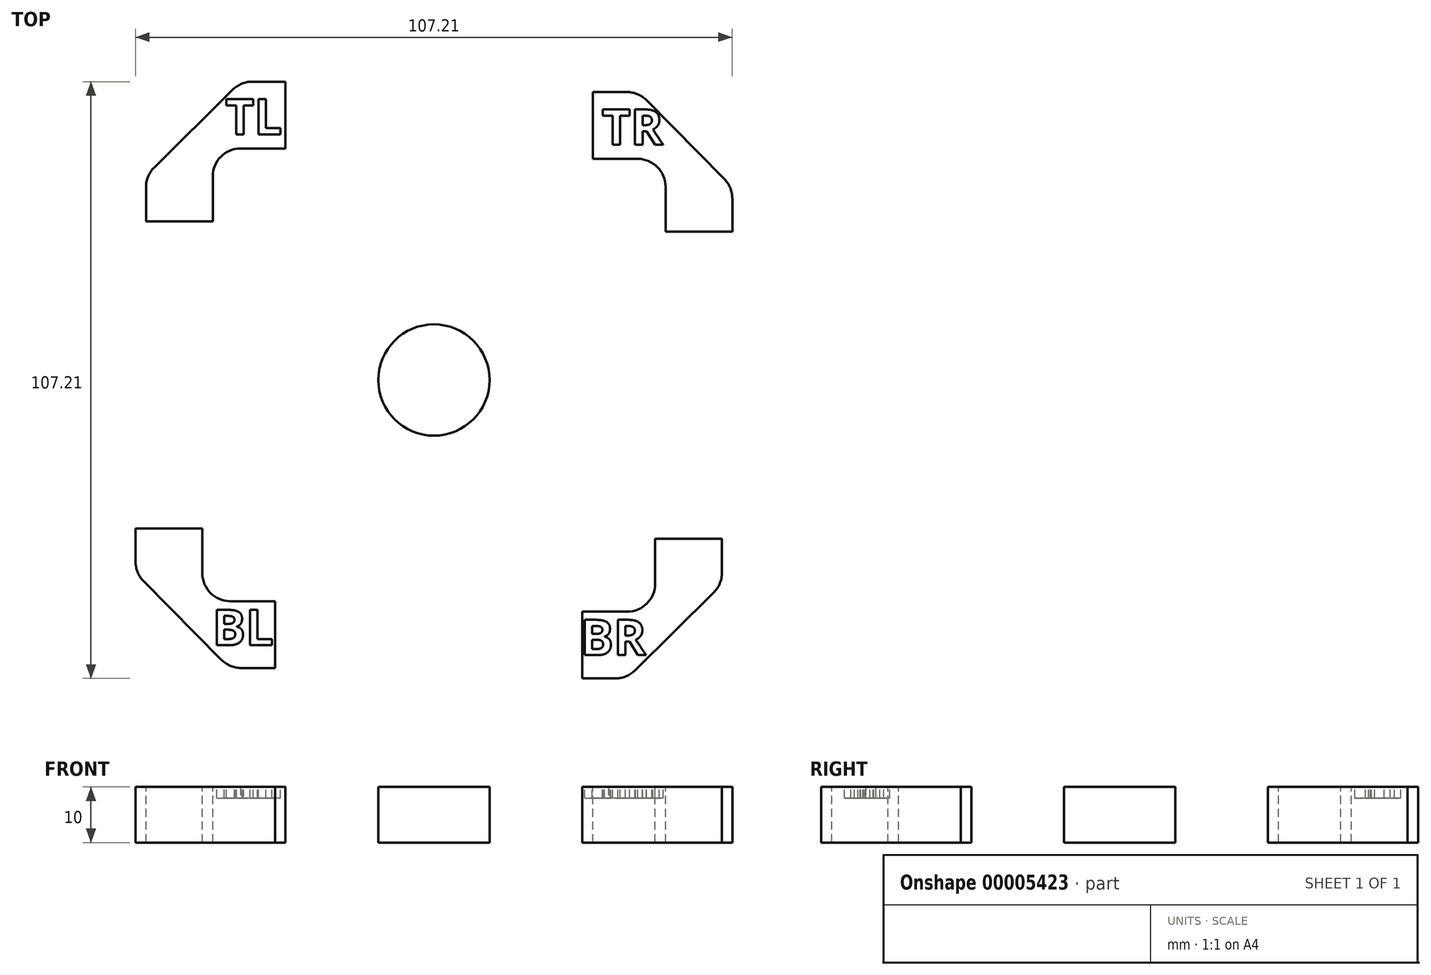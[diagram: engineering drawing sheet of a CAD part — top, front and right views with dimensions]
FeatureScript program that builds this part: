
annotation { "Feature Type Name" : "Feature", "Feature Type Description" : "" }
export const myFeature = defineFeature(function(context is Context, id is Id, definition is map)
    precondition{}
    {
        {
            var Q0;
            Q0=qCreatedBy(makeId("Top.planeOp"),FACE);
            var sketch = newSketch(context, id + "F0", { "sketchPlane" : qUnion([Q0])});
            skPoint(sketch, "E0.rect.middle", {"position": v(0, 0) * mm});
            skLineSegment(sketch, "E1.top", {"start": v(28.56, 51.77) * mm, "end": v(34.68, 51.77) * mm});
            skLineSegment(sketch, "E2.bottom", {"start": v(34.68, 51.77) * mm, "end": v(28.56, 51.77) * mm});
            skLineSegment(sketch, "E2.top", {"start": v(53.64, 26.7) * mm, "end": v(41.64, 26.7) * mm});
            skLineSegment(sketch, "E2.left", {"start": v(53.64, 32.66) * mm, "end": v(53.64, 26.7) * mm});
            skLineSegment(sketch, "E2.right", {"start": v(28.56, 51.77) * mm, "end": v(28.56, 39.77) * mm});
            skLineSegment(sketch, "E3.bottom", {"start": v(28.56, 39.77) * mm, "end": v(36.64, 39.77) * mm});
            skLineSegment(sketch, "E3.right", {"start": v(41.64, 34.77) * mm, "end": v(41.64, 26.7) * mm});
            skPoint(sketch, "E4.orphan", {"position": v(44.55, 51.77) * mm});
            skPoint(sketch, "E5.orphan", {"position": v(53.64, 51.77) * mm});
            skPoint(sketch, "E6.visualSharp", {"position": v(41.64, 39.77) * mm});
            skArc(sketch, "E6.filletArc", {"start": v(41.64, 34.77) * mm, "mid": v(40.18, 38.3) * mm, "end": v(36.64, 39.77) * mm});
            skPoint(sketch, "E7.visualSharp", {"position": v(36.67, 51.77) * mm});
            skArc(sketch, "E7.filletArc", {"start": v(38.22, 50.3) * mm, "mid": v(36.6, 51.4) * mm, "end": v(34.68, 51.77) * mm});
            skPoint(sketch, "E8.visualSharp", {"position": v(53.64, 34.62) * mm});
            skArc(sketch, "E8.filletArc", {"start": v(53.64, 32.66) * mm, "mid": v(53.27, 34.55) * mm, "end": v(52.21, 36.16) * mm});
            skLineSegment(sketch, "E9", {"start": v(38.22, 50.3) * mm, "end": v(52.21, 36.16) * mm});
            skPoint(sketch, "E10.1.0", {"position": v(-51.7, 36.67) * mm});
            skPoint(sketch, "E10.1.1", {"position": v(-39.7, 41.64) * mm});
            skPoint(sketch, "E10.1.2", {"position": v(-51.7, 44.55) * mm});
            skLineSegment(sketch, "E10.1.3", {"start": v(-50.24, 38.22) * mm, "end": v(-36.09, 52.21) * mm});
            skLineSegment(sketch, "E10.1.4", {"start": v(-34.7, 41.64) * mm, "end": v(-26.62, 41.64) * mm});
            skLineSegment(sketch, "E10.1.5", {"start": v(-51.7, 28.56) * mm, "end": v(-39.7, 28.56) * mm});
            skLineSegment(sketch, "E10.1.6", {"start": v(-39.7, 28.56) * mm, "end": v(-39.7, 36.64) * mm});
            skLineSegment(sketch, "E10.1.7", {"start": v(-26.62, 53.64) * mm, "end": v(-26.62, 41.64) * mm});
            skLineSegment(sketch, "E10.1.8", {"start": v(-32.59, 53.64) * mm, "end": v(-26.62, 53.64) * mm});
            skLineSegment(sketch, "E10.1.9", {"start": v(-51.7, 34.68) * mm, "end": v(-51.7, 28.56) * mm});
            skPoint(sketch, "E10.1.10", {"position": v(-34.55, 53.64) * mm});
            skPoint(sketch, "E10.1.11", {"position": v(-51.7, 53.64) * mm});
            skArc(sketch, "E10.1.12", {"start": v(-50.24, 38.22) * mm, "mid": v(-51.32, 36.6) * mm, "end": v(-51.7, 34.68) * mm});
            skArc(sketch, "E10.1.13", {"start": v(-32.59, 53.64) * mm, "mid": v(-34.48, 53.27) * mm, "end": v(-36.09, 52.21) * mm});
            skArc(sketch, "E10.1.14", {"start": v(-34.7, 41.64) * mm, "mid": v(-38.24, 40.18) * mm, "end": v(-39.7, 36.64) * mm});
            skPoint(sketch, "E10.2.0", {"position": v(-36.6, -51.7) * mm});
            skPoint(sketch, "E10.2.1", {"position": v(-41.57, -39.7) * mm});
            skPoint(sketch, "E10.2.2", {"position": v(-44.48, -51.7) * mm});
            skLineSegment(sketch, "E10.2.3", {"start": v(-38.15, -50.24) * mm, "end": v(-52.14, -36.09) * mm});
            skLineSegment(sketch, "E10.2.4", {"start": v(-41.57, -34.7) * mm, "end": v(-41.57, -26.62) * mm});
            skLineSegment(sketch, "E10.2.5", {"start": v(-28.5, -51.7) * mm, "end": v(-28.5, -39.7) * mm});
            skLineSegment(sketch, "E10.2.6", {"start": v(-28.5, -39.7) * mm, "end": v(-36.57, -39.7) * mm});
            skLineSegment(sketch, "E10.2.7", {"start": v(-53.57, -26.62) * mm, "end": v(-41.57, -26.62) * mm});
            skLineSegment(sketch, "E10.2.8", {"start": v(-53.57, -32.59) * mm, "end": v(-53.57, -26.62) * mm});
            skLineSegment(sketch, "E10.2.9", {"start": v(-34.61, -51.7) * mm, "end": v(-28.5, -51.7) * mm});
            skPoint(sketch, "E10.2.10", {"position": v(-53.57, -34.55) * mm});
            skPoint(sketch, "E10.2.11", {"position": v(-53.57, -51.7) * mm});
            skArc(sketch, "E10.2.12", {"start": v(-38.15, -50.24) * mm, "mid": v(-36.53, -51.32) * mm, "end": v(-34.61, -51.7) * mm});
            skArc(sketch, "E10.2.13", {"start": v(-53.57, -32.59) * mm, "mid": v(-53.2, -34.48) * mm, "end": v(-52.14, -36.09) * mm});
            skArc(sketch, "E10.2.14", {"start": v(-41.57, -34.7) * mm, "mid": v(-40.1, -38.24) * mm, "end": v(-36.57, -39.7) * mm});
            skPoint(sketch, "E10.3.0", {"position": v(51.77, -36.6) * mm});
            skPoint(sketch, "E10.3.1", {"position": v(39.77, -41.57) * mm});
            skPoint(sketch, "E10.3.2", {"position": v(51.77, -44.48) * mm});
            skLineSegment(sketch, "E10.3.3", {"start": v(50.3, -38.15) * mm, "end": v(36.16, -52.14) * mm});
            skLineSegment(sketch, "E10.3.4", {"start": v(34.77, -41.57) * mm, "end": v(26.7, -41.57) * mm});
            skLineSegment(sketch, "E10.3.5", {"start": v(51.77, -28.5) * mm, "end": v(39.77, -28.5) * mm});
            skLineSegment(sketch, "E10.3.6", {"start": v(39.77, -28.5) * mm, "end": v(39.77, -36.57) * mm});
            skLineSegment(sketch, "E10.3.7", {"start": v(26.7, -53.57) * mm, "end": v(26.7, -41.57) * mm});
            skLineSegment(sketch, "E10.3.8", {"start": v(32.66, -53.57) * mm, "end": v(26.7, -53.57) * mm});
            skLineSegment(sketch, "E10.3.9", {"start": v(51.77, -34.61) * mm, "end": v(51.77, -28.5) * mm});
            skPoint(sketch, "E10.3.10", {"position": v(34.62, -53.57) * mm});
            skPoint(sketch, "E10.3.11", {"position": v(51.77, -53.57) * mm});
            skArc(sketch, "E10.3.12", {"start": v(50.3, -38.15) * mm, "mid": v(51.4, -36.53) * mm, "end": v(51.77, -34.61) * mm});
            skArc(sketch, "E10.3.13", {"start": v(32.66, -53.57) * mm, "mid": v(34.55, -53.2) * mm, "end": v(36.16, -52.14) * mm});
            skArc(sketch, "E10.3.14", {"start": v(34.77, -41.57) * mm, "mid": v(38.3, -40.1) * mm, "end": v(39.77, -36.57) * mm});
            skPoint(sketch, "E10.center", {"position": v(0.04, 0.04) * mm});
            skCircle(sketch, "E11", {"center": v(0.04, 0.04) * mm, "radius": 10 * mm});
            skText(sketch, "E12", { "text": "TL", "fontName": "OpenSans-Bold.ttf"});
            skText(sketch, "E13", { "text": "TR", "fontName": "OpenSans-Bold.ttf"});
            skText(sketch, "E14", { "text": "BL", "fontName": "OpenSans-Bold.ttf"});
            skText(sketch, "E15", { "text": "BR", "fontName": "OpenSans-Bold.ttf"});
            const initialGuessF0  = {"E12": [-0.03741, 0.04417, 1, 0, 0.0064], "E13": [0.03022, 0.0423, 1, 0, 0.0064], "E14": [-0.03977, -0.0476, 1, 0, 0.0064], "E15": [0.02633, -0.0494, 1, 0, 0.0064]};
            skSetInitialGuess(sketch, initialGuessF0);
            skSolve(sketch);
        }
        {
            var Q0;
            Q0=makeQuery(id+"F0.imprint","IMPRINT",FACE,{"disambiguationData":[TD([[makeQuery(id+"F0.imprint","IMPRINT",EDGE,{"derivedFrom":sQuery(id+"F0.wireOp",EDGE,"E10.1.3")}),-1.0]])]});
            var Q1;
            Q1=makeQuery(id+"F0.imprint","IMPRINT",FACE,{"disambiguationData":[TD([[makeQuery(id+"F0.imprint","IMPRINT",EDGE,{"derivedFrom":sQuery(id+"F0.wireOp",EDGE,"E2.bottom")}),1.0]])]});
            var Q2;
            Q2=makeQuery(id+"F0.imprint","IMPRINT",FACE,{"disambiguationData":[TD([[makeQuery(id+"F0.imprint","IMPRINT",EDGE,{"derivedFrom":sQuery(id+"F0.wireOp",EDGE,"E10.2.3")}),-1.0]])]});
            var Q3;
            Q3=makeQuery(id+"F0.imprint","IMPRINT",FACE,{"disambiguationData":[TD([[makeQuery(id+"F0.imprint","IMPRINT",EDGE,{"derivedFrom":sQuery(id+"F0.wireOp",EDGE,"E10.3.3")}),-1.0]])]});
            var Q4;
            Q4=makeQuery(id+"F0.imprint","IMPRINT",FACE,{"disambiguationData":[TD([[makeQuery(id+"F0.imprint","IMPRINT",EDGE,{"derivedFrom":sQuery(id+"F0.wireOp",EDGE,"E11")}),1.0]])]});
            var Q5;
            Q5=makeQuery(id+"F0.imprint","IMPRINT",FACE,{"disambiguationData":[TD([[makeQuery(id+"F0.imprint","IMPRINT",EDGE,{"derivedFrom":sQuery(id+"F0.wireOp",EDGE,"E12.sketch_text.stroke-8")}),-1.0]])]});
            var Q6;
            Q6=makeQuery(id+"F0.imprint","IMPRINT",FACE,{"disambiguationData":[TD([[makeQuery(id+"F0.imprint","IMPRINT",EDGE,{"derivedFrom":sQuery(id+"F0.wireOp",EDGE,"E12.sketch_text.stroke-0")}),-1.0]])]});
            var Q7;
            Q7=makeQuery(id+"F0.imprint","IMPRINT",FACE,{"disambiguationData":[TD([[makeQuery(id+"F0.imprint","IMPRINT",EDGE,{"derivedFrom":sQuery(id+"F0.wireOp",EDGE,"E13.sketch_text.stroke-8")}),1.0]])]});
            var Q8;
            Q8=makeQuery(id+"F0.imprint","IMPRINT",FACE,{"disambiguationData":[TD([[makeQuery(id+"F0.imprint","IMPRINT",EDGE,{"derivedFrom":sQuery(id+"F0.wireOp",EDGE,"E13.sketch_text.stroke-0")}),-1.0]])]});
            var Q9;
            Q9=makeQuery(id+"F0.imprint","IMPRINT",FACE,{"disambiguationData":[TD([[makeQuery(id+"F0.imprint","IMPRINT",EDGE,{"derivedFrom":sQuery(id+"F0.wireOp",EDGE,"E13.sketch_text.stroke-8")}),-1.0]])]});
            var Q10;
            Q10=makeQuery(id+"F0.imprint","IMPRINT",FACE,{"disambiguationData":[TD([[makeQuery(id+"F0.imprint","IMPRINT",EDGE,{"derivedFrom":sQuery(id+"F0.wireOp",EDGE,"E15.sketch_text.stroke-25")}),1.0]])]});
            var Q11;
            Q11=makeQuery(id+"F0.imprint","IMPRINT",FACE,{"disambiguationData":[TD([[makeQuery(id+"F0.imprint","IMPRINT",EDGE,{"derivedFrom":sQuery(id+"F0.wireOp",EDGE,"E15.sketch_text.stroke-12")}),1.0]])]});
            var Q12;
            Q12=makeQuery(id+"F0.imprint","IMPRINT",FACE,{"disambiguationData":[TD([[makeQuery(id+"F0.imprint","IMPRINT",EDGE,{"derivedFrom":sQuery(id+"F0.wireOp",EDGE,"E15.sketch_text.stroke-19")}),1.0]])]});
            var Q13;
            Q13=makeQuery(id+"F0.imprint","IMPRINT",FACE,{"disambiguationData":[TD([[makeQuery(id+"F0.imprint","IMPRINT",EDGE,{"derivedFrom":sQuery(id+"F0.wireOp",EDGE,"E15.sketch_text.stroke-0")}),-1.0]])]});
            var Q14;
            Q14=makeQuery(id+"F0.imprint","IMPRINT",FACE,{"disambiguationData":[TD([[makeQuery(id+"F0.imprint","IMPRINT",EDGE,{"derivedFrom":sQuery(id+"F0.wireOp",EDGE,"E15.sketch_text.stroke-25")}),-1.0]])]});
            var Q15;
            Q15 = qSketchRegion(id + "F0", true);
            var Q16;
            Q16=makeQuery(id+"F0.imprint","IMPRINT",FACE,{"disambiguationData":[TD([[makeQuery(id+"F0.imprint","IMPRINT",EDGE,{"derivedFrom":sQuery(id+"F0.wireOp",EDGE,"E14.sketch_text.stroke-25")}),-1.0]])]});
            var Q17;
            Q17=makeQuery(id+"F0.imprint","IMPRINT",FACE,{"disambiguationData":[TD([[makeQuery(id+"F0.imprint","IMPRINT",EDGE,{"derivedFrom":sQuery(id+"F0.wireOp",EDGE,"E14.sketch_text.stroke-19")}),1.0]])]});
            var Q18;
            Q18=makeQuery(id+"F0.imprint","IMPRINT",FACE,{"disambiguationData":[TD([[makeQuery(id+"F0.imprint","IMPRINT",EDGE,{"derivedFrom":sQuery(id+"F0.wireOp",EDGE,"E14.sketch_text.stroke-12")}),1.0]])]});
            var Q19;
            Q19=makeQuery(id+"F0.imprint","IMPRINT",FACE,{"disambiguationData":[TD([[makeQuery(id+"F0.imprint","IMPRINT",EDGE,{"derivedFrom":sQuery(id+"F0.wireOp",EDGE,"E14.sketch_text.stroke-0")}),-1.0]])]});
            extrude(context, id + "F1", {"entities" : qUnion([Q0, Q1, Q2, Q3, Q4, Q5, Q6, Q7, Q8, Q9, Q10, Q11, Q12, Q13, Q14, Q15, Q16, Q17, Q18, Q19]), "oppositeDirection" : true, "depth" : 10 * mm});
        }
        {
            var Q0;
            Q0=makeQuery(id+"F0.imprint","IMPRINT",FACE,{"disambiguationData":[TD([[makeQuery(id+"F0.imprint","IMPRINT",EDGE,{"derivedFrom":sQuery(id+"F0.wireOp",EDGE,"E15.sketch_text.stroke-25")}),-1.0]])]});
            var Q1;
            Q1=makeQuery(id+"F0.imprint","IMPRINT",FACE,{"disambiguationData":[TD([[makeQuery(id+"F0.imprint","IMPRINT",EDGE,{"derivedFrom":sQuery(id+"F0.wireOp",EDGE,"E15.sketch_text.stroke-0")}),-1.0]])]});
            var Q2;
            Q2=makeQuery(id+"F0.imprint","IMPRINT",FACE,{"disambiguationData":[TD([[makeQuery(id+"F0.imprint","IMPRINT",EDGE,{"derivedFrom":sQuery(id+"F0.wireOp",EDGE,"E14.sketch_text.stroke-25")}),-1.0]])]});
            var Q3;
            Q3=makeQuery(id+"F0.imprint","IMPRINT",FACE,{"disambiguationData":[TD([[makeQuery(id+"F0.imprint","IMPRINT",EDGE,{"derivedFrom":sQuery(id+"F0.wireOp",EDGE,"E14.sketch_text.stroke-0")}),-1.0]])]});
            var Q4;
            Q4=makeQuery(id+"F0.imprint","IMPRINT",FACE,{"disambiguationData":[TD([[makeQuery(id+"F0.imprint","IMPRINT",EDGE,{"derivedFrom":sQuery(id+"F0.wireOp",EDGE,"E12.sketch_text.stroke-0")}),-1.0]])]});
            var Q5;
            Q5=makeQuery(id+"F0.imprint","IMPRINT",FACE,{"disambiguationData":[TD([[makeQuery(id+"F0.imprint","IMPRINT",EDGE,{"derivedFrom":sQuery(id+"F0.wireOp",EDGE,"E12.sketch_text.stroke-8")}),-1.0]])]});
            var Q6;
            Q6=makeQuery(id+"F0.imprint","IMPRINT",FACE,{"disambiguationData":[TD([[makeQuery(id+"F0.imprint","IMPRINT",EDGE,{"derivedFrom":sQuery(id+"F0.wireOp",EDGE,"E13.sketch_text.stroke-0")}),-1.0]])]});
            var Q7;
            Q7=makeQuery(id+"F0.imprint","IMPRINT",FACE,{"disambiguationData":[TD([[makeQuery(id+"F0.imprint","IMPRINT",EDGE,{"derivedFrom":sQuery(id+"F0.wireOp",EDGE,"E13.sketch_text.stroke-8")}),-1.0]])]});
            extrude(context, id + "F2", {"entities" : qUnion([Q0, Q1, Q2, Q3, Q4, Q5, Q6, Q7]), "operationType" : NewBodyOperationType.REMOVE, "oppositeDirection" : true, "depth" : 2 * mm});
        }
        {
            var Q0;
            Q0=makeQuery(id+"F0.imprint","IMPRINT",FACE,{"disambiguationData":[TD([[makeQuery(id+"F0.imprint","IMPRINT",EDGE,{"derivedFrom":sQuery(id+"F0.wireOp",EDGE,"E13.sketch_text.stroke-0")}),-1.0]])]});
            var Q1;
            Q1=makeQuery(id+"F0.imprint","IMPRINT",FACE,{"disambiguationData":[TD([[makeQuery(id+"F0.imprint","IMPRINT",EDGE,{"derivedFrom":sQuery(id+"F0.wireOp",EDGE,"E13.sketch_text.stroke-8")}),-1.0]])]});
            extrude(context, id + "F3", {"entities" : qUnion([Q0, Q1]), "operationType" : NewBodyOperationType.REMOVE, "oppositeDirection" : true, "depth" : 2 * mm});
        }
        {
            var Q0;
            Q0=makeQuery(id+"F0.imprint","IMPRINT",FACE,{"disambiguationData":[TD([[makeQuery(id+"F0.imprint","IMPRINT",EDGE,{"derivedFrom":sQuery(id+"F0.wireOp",EDGE,"E15.sketch_text.stroke-0")}),-1.0]])]});
            var Q1;
            Q1=makeQuery(id+"F0.imprint","IMPRINT",FACE,{"disambiguationData":[TD([[makeQuery(id+"F0.imprint","IMPRINT",EDGE,{"derivedFrom":sQuery(id+"F0.wireOp",EDGE,"E15.sketch_text.stroke-25")}),-1.0]])]});
            extrude(context, id + "F4", {"entities" : qUnion([Q0, Q1]), "operationType" : NewBodyOperationType.REMOVE, "oppositeDirection" : true, "depth" : 2 * mm});
        }
        {
            var Q0;
            Q0=makeQuery(id+"F0.imprint","IMPRINT",FACE,{"disambiguationData":[TD([[makeQuery(id+"F0.imprint","IMPRINT",EDGE,{"derivedFrom":sQuery(id+"F0.wireOp",EDGE,"E14.sketch_text.stroke-0")}),-1.0]])]});
            var Q1;
            Q1=makeQuery(id+"F0.imprint","IMPRINT",FACE,{"disambiguationData":[TD([[makeQuery(id+"F0.imprint","IMPRINT",EDGE,{"derivedFrom":sQuery(id+"F0.wireOp",EDGE,"E14.sketch_text.stroke-25")}),-1.0]])]});
            extrude(context, id + "F5", {"entities" : qUnion([Q0, Q1]), "operationType" : NewBodyOperationType.REMOVE, "oppositeDirection" : true, "depth" : 2 * mm});
        }
    });
